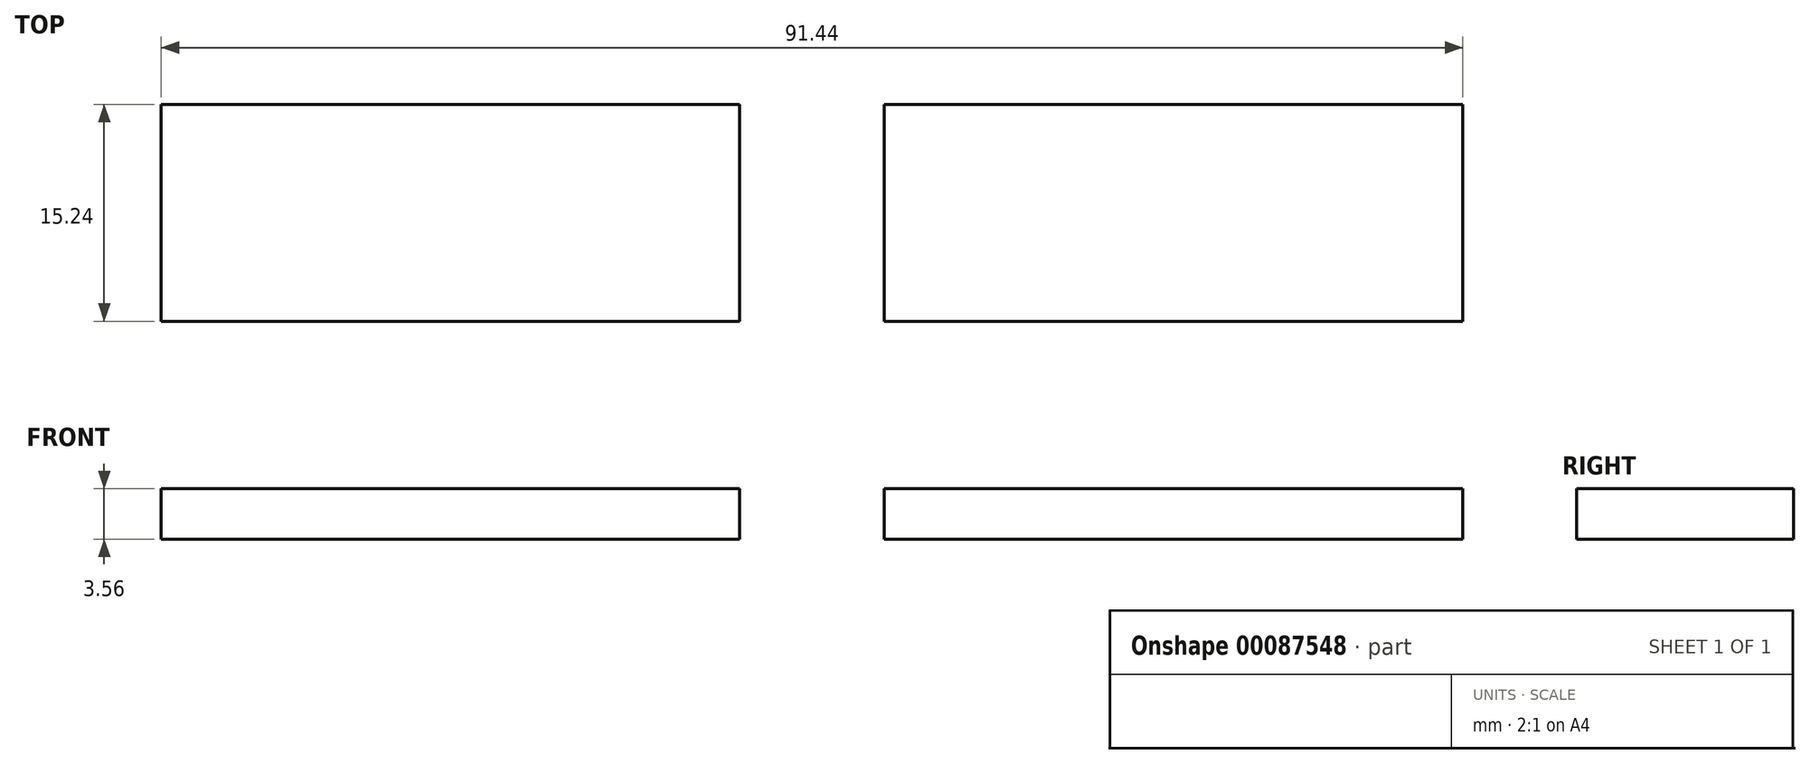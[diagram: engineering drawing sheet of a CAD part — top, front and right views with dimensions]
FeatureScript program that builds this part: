
annotation { "Feature Type Name" : "Feature", "Feature Type Description" : "" }
export const myFeature = defineFeature(function(context is Context, id is Id, definition is map)
    precondition{}
    {
        {
            var Q0;
            Q0=qCreatedBy(makeId("Top.planeOp"),FACE);
            var sketch = newSketch(context, id + "F0", { "sketchPlane" : qUnion([Q0])});
            skLineSegment(sketch, "E0.bottom", {"start": v(0, 0) * mm, "end": v(40.64, 0) * mm});
            skLineSegment(sketch, "E0.top", {"start": v(0, 15.24) * mm, "end": v(40.64, 15.24) * mm});
            skLineSegment(sketch, "E0.left", {"start": v(0, 0) * mm, "end": v(0, 15.24) * mm});
            skLineSegment(sketch, "E0.right", {"start": v(40.64, 0) * mm, "end": v(40.64, 15.24) * mm});
            skLineSegment(sketch, "E1", {"start": v(-5.08, 25.98) * mm, "end": v(-5.08, -26.45) * mm, "construction": true});
            skLineSegment(sketch, "E2.MirrorCS", {"start": v(-10.16, 15.24) * mm, "end": v(-50.8, 15.24) * mm});
            skLineSegment(sketch, "E3.MirrorCS", {"start": v(-10.16, 0) * mm, "end": v(-10.16, 15.24) * mm});
            skLineSegment(sketch, "E4.MirrorCS", {"start": v(-10.16, 0) * mm, "end": v(-50.8, 0) * mm});
            skLineSegment(sketch, "E5.MirrorCS", {"start": v(-50.8, 0) * mm, "end": v(-50.8, 15.24) * mm});
            skSolve(sketch);
        }
        {
            var Q0;
            Q0=qSketchRegion(id+"F0",true);
            extrude(context, id + "F1", {"entities" : qUnion([Q0]), "depth" : 3.56 * mm});
        }
    });
